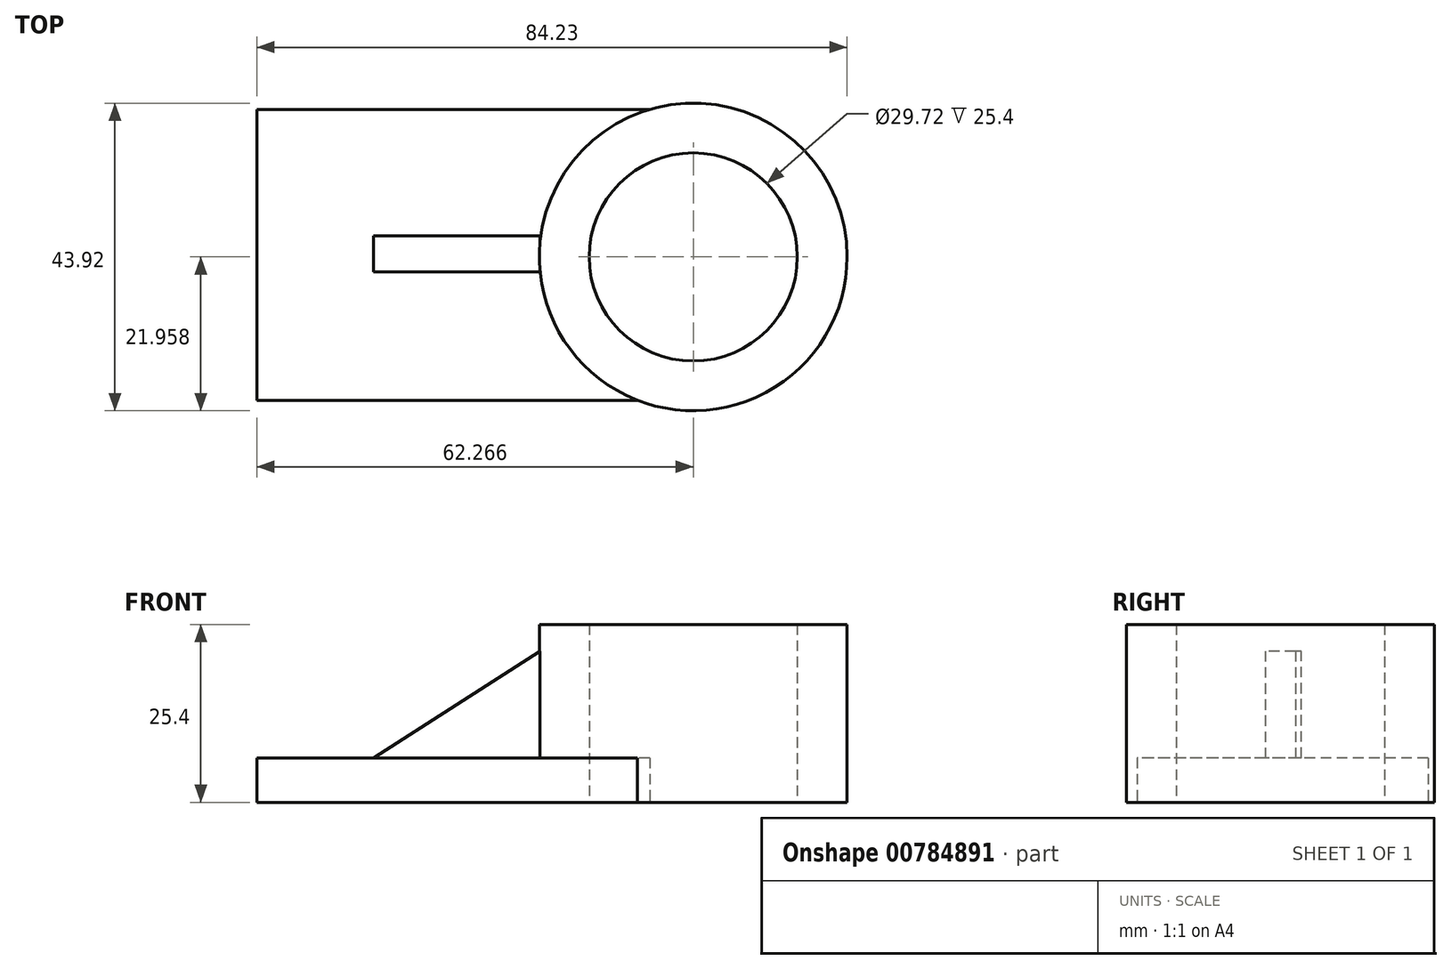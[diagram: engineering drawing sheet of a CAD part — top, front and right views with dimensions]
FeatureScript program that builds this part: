
annotation { "Feature Type Name" : "Feature", "Feature Type Description" : "" }
export const myFeature = defineFeature(function(context is Context, id is Id, definition is map)
    precondition{}
    {
        {
            var Q0;
            Q0=qCreatedBy(makeId("Top.planeOp"),FACE);
            var sketch = newSketch(context, id + "F0", { "sketchPlane" : qUnion([Q0])});
            skCircle(sketch, "E0", {"center": v(25.12, 10.68) * mm, "radius": 21.96 * mm});
            skLineSegment(sketch, "E1.bottom", {"start": v(18.9, 31.74) * mm, "end": v(-37.15, 31.74) * mm});
            skLineSegment(sketch, "E1.top", {"start": v(18.9, -9.78) * mm, "end": v(-37.15, -9.78) * mm});
            skLineSegment(sketch, "E1.left", {"start": v(18.9, 31.74) * mm, "end": v(18.9, -9.78) * mm});
            skLineSegment(sketch, "E1.right", {"start": v(-37.15, 31.74) * mm, "end": v(-37.15, -9.78) * mm});
            skCircle(sketch, "E2", {"center": v(25.12, 10.68) * mm, "radius": 14.86 * mm});
            skSolve(sketch);
        }
        {
            var Q0;
            {var subQ0=sQuery(id+"F0.wireOp",EDGE,"E1.left");Q0=makeQuery(id+"F0.imprint","IMPRINT",FACE,{"disambiguationData":[TD([[makeQuery(id+"F0.imprint","IMPRINT",EDGE,{"derivedFrom":subQ0}),-1.0]])]});}
            var Q1;
            {var subQ0=sQuery(id+"F0.wireOp",EDGE,"E1.left");Q1=makeQuery(id+"F0.imprint","IMPRINT",FACE,{"disambiguationData":[TD([[makeQuery(id+"F0.imprint","IMPRINT",EDGE,{"derivedFrom":subQ0}),1.0]])]});}
            extrude(context, id + "F1", {"entities" : qUnion([Q0, Q1]), "depth" : 25.4 * mm, "offsetDistance" : 25.4 * mm});
        }
        {
            var Q0;
            Q0 = qSketchRegion(id + "F0", true);
            extrude(context, id + "F2", {"entities" : qUnion([Q0]), "operationType" : NewBodyOperationType.ADD, "depth" : 6.35 * mm, "offsetDistance" : 25.4 * mm});
        }
        {
            var Q0;
            Q0=makeQuery(id+"F2.opExtrude","CAP_FACE",FACE,{"disambiguationData":[OSD([sQuery(id+"F0.wireOp",EDGE,"E0"),sQuery(id+"F0.wireOp",EDGE,"E1.bottom"),sQuery(id+"F0.wireOp",EDGE,"E1.top"),sQuery(id+"F0.wireOp",EDGE,"E1.right"),sQuery(id+"F0.wireOp",EDGE,"E2")])],"isStart":false});
            var sketch = newSketch(context, id + "F3", { "sketchPlane" : qUnion([Q0])});
            skLineSegment(sketch, "E3.bottom", {"start": v(-20.48, 13.67) * mm, "end": v(3.26, 13.67) * mm});
            skLineSegment(sketch, "E3.top", {"start": v(-20.48, 8.52) * mm, "end": v(3.26, 8.52) * mm});
            skLineSegment(sketch, "E3.left", {"start": v(-20.48, 13.67) * mm, "end": v(-20.48, 8.52) * mm});
            skLineSegment(sketch, "E3.right", {"start": v(3.26, 13.67) * mm, "end": v(3.26, 8.52) * mm});
            skSolve(sketch);
        }
        {
            var Q0;
            Q0 = qSketchRegion(id + "F3", true);
            extrude(context, id + "F4", {"entities" : qUnion([Q0]), "operationType" : NewBodyOperationType.ADD, "depth" : 15.24 * mm, "offsetDistance" : 25.4 * mm});
        }
        {
            var Q0;
            Q0=makeQuery(id+"F4.opExtrude","SWEPT_FACE",FACE,{"disambiguationData":[OSD([sQuery(id+"F3.wireOp",EDGE,"E3.top")])]});
            var sketch = newSketch(context, id + "F5", { "sketchPlane" : qUnion([Q0])});
            skLineSegment(sketch, "E4", {"start": v(3.26, 21.6) * mm, "end": v(-20.48, 6.35) * mm});
            skSolve(sketch);
        }
        {
            var Q0;
            Q0=makeQuery(id+"F5.imprint","IMPRINT",FACE,{"disambiguationData":[TD([[makeQuery(id+"F5.imprint","IMPRINT",EDGE,{"derivedFrom":sQuery(id+"F5.wireOp",EDGE,"E4")}),-1.0]])]});
            extrude(context, id + "F6", {"entities" : qUnion([Q0]), "operationType" : NewBodyOperationType.REMOVE, "oppositeDirection" : true, "depth" : 25.4 * mm, "offsetDistance" : 25.4 * mm});
        }
    });
